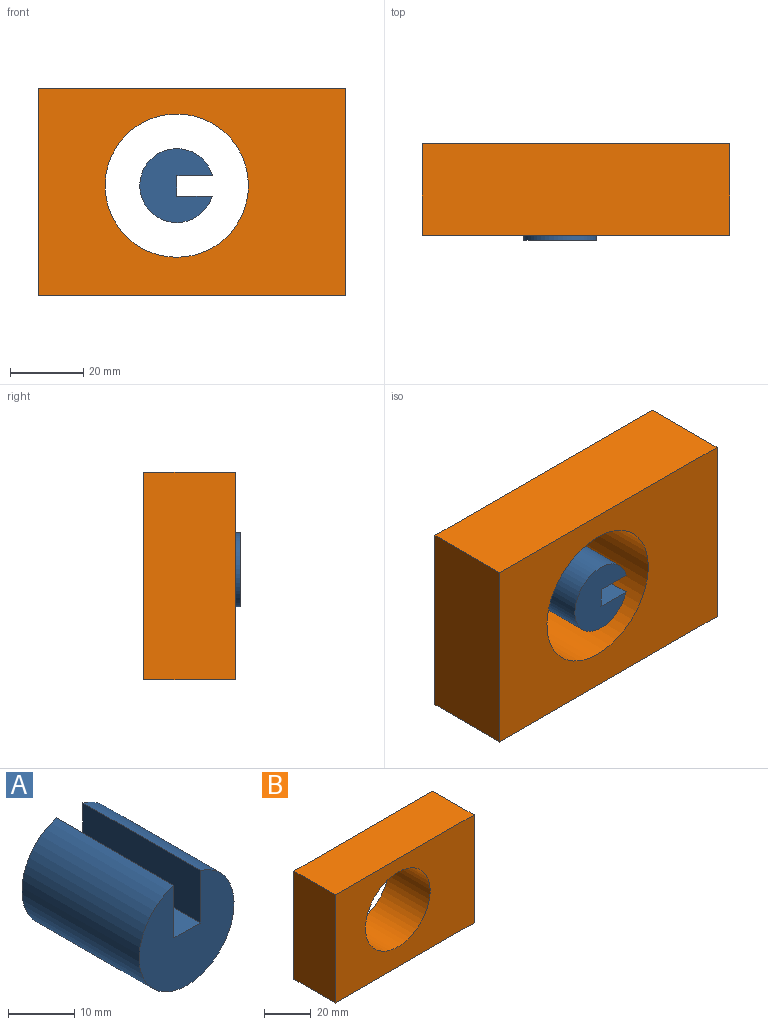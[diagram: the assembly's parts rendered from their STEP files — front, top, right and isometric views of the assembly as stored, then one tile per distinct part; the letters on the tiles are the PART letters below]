
ASSEMBLY  parts=2 mates=1
PART A: 6 faces, bbox 20.2x25x19.8 mm
  f0: cylinder r=10.1mm len=25mm, axis (0,1,0), area 1445.4mm2, adj f1,f2,f3,f5
  f1: plane 20.21x19.84mm, normal (0,-1,0), area 265.1mm2, adj f0,f3,f4,f5
  f2: plane 20.21x19.84mm, normal (0,1,0), area 265.1mm2, adj f0,f3,f4,f5
  f3: plane 25x9.68mm, normal (1,0,0), area 241.9mm2, adj f0,f1,f2,f4
  f4: plane 25x5.6mm, normal (0.01,0,1), area 139.9mm2, adj f1,f2,f3,f5
  f5: plane 25x9.68mm, normal (-1,0,0), area 242mm2, adj f0,f1,f2,f4
PART B: 7 faces, bbox 84x25x56.6 mm
  f0: plane 83.96x25mm, normal (0,0,1), area 2099mm2, adj f1,f4,f5,f6
  f1: plane 56.6x25mm, normal (-1,0,0), area 1415mm2, adj f0,f2,f5,f6
  f2: plane 83.96x25mm, normal (0,0,-1), area 2099mm2, adj f1,f4,f5,f6
  f3: cylinder r=19.57mm len=39.14mm, axis (0,1,0), area 3074.1mm2, adj f5,f6
  f4: plane 56.6x25mm, normal (1,0,0), area 1415mm2, adj f0,f2,f5,f6
  f5: plane 83.96x56.6mm, normal (0,-1,0), area 3548.9mm2, adj f0,f1,f2,f3,f4
  f6: plane 83.96x56.6mm, normal (0,1,0), area 3548.9mm2, adj f0,f1,f2,f3,f4
PLACE A rot(axis=(0,1,0),90deg) t=(-112.47,27.81,19.64)mm
PLACE B t=(-72.01,29.13,-6.72)mm fixed
MATE slider B.f3 <-> A.f0  axis (0,1,0) through (-57.61,16.63,80.19)mm
